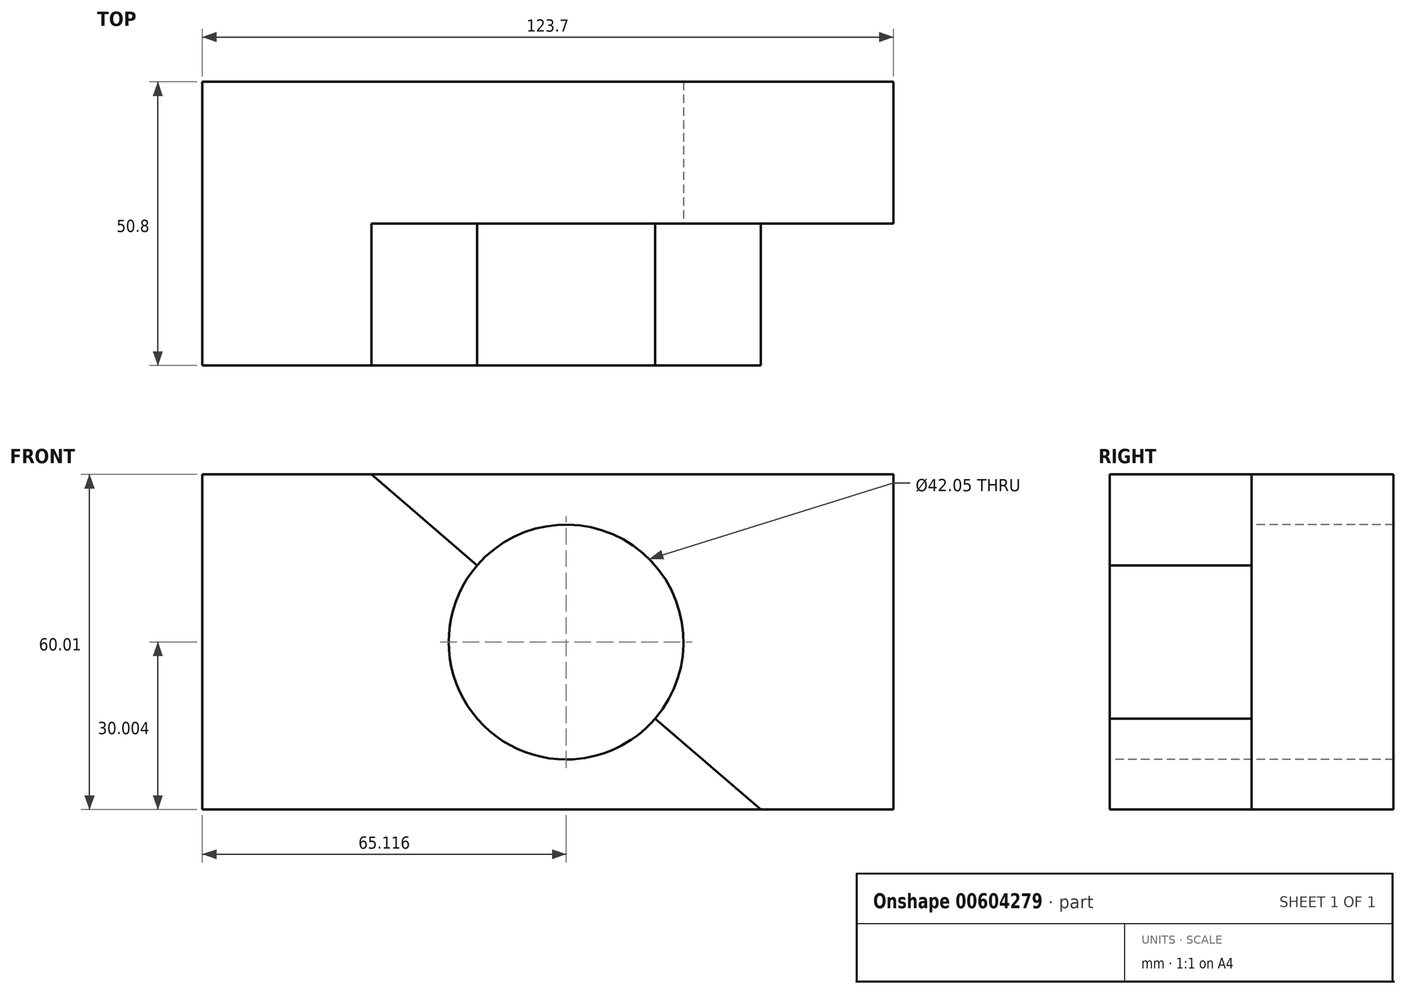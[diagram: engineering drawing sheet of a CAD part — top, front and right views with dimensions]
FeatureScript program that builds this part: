
annotation { "Feature Type Name" : "Feature", "Feature Type Description" : "" }
export const myFeature = defineFeature(function(context is Context, id is Id, definition is map)
    precondition{}
    {
        {
            var Q0;
            Q0=qCreatedBy(makeId("Front.planeOp"),FACE);
            var sketch = newSketch(context, id + "F0", { "sketchPlane" : qUnion([Q0])});
            skLineSegment(sketch, "E0.bottom", {"start": v(-74.58, 0) * mm, "end": v(23.72, 0) * mm});
            skLineSegment(sketch, "E0.top", {"start": v(-74.58, 60) * mm, "end": v(23.72, 60) * mm});
            skLineSegment(sketch, "E0.left", {"start": v(-74.58, 0) * mm, "end": v(-74.58, 60) * mm});
            skLineSegment(sketch, "E0.right", {"start": v(23.72, 0) * mm, "end": v(23.72, 60) * mm});
            skSolve(sketch);
        }
        {
            var Q0;
            Q0=makeQuery(id+"F0.imprint","IMPRINT",FACE,{"disambiguationData":[TD([[makeQuery(id+"F0.imprint","IMPRINT",EDGE,{"derivedFrom":sQuery(id+"F0.wireOp",EDGE,"E0.bottom")}),1.0]])]});
            extrude(context, id + "F1", {"entities" : qUnion([Q0]), "depth" : 25.4 * mm, "offsetDistance" : 25.4 * mm});
        }
        {
            var Q0;
            Q0=makeQuery(id+"F1.opExtrude","CAP_FACE",FACE,{"disambiguationData":[OSD([sQuery(id+"F0.wireOp",EDGE,"E0.bottom"),sQuery(id+"F0.wireOp",EDGE,"E0.top"),sQuery(id+"F0.wireOp",EDGE,"E0.left"),sQuery(id+"F0.wireOp",EDGE,"E0.right")])],"isStart":false});
            extrude(context, id + "F2", {"entities" : qUnion([Q0]), "operationType" : NewBodyOperationType.ADD, "depth" : 25.4 * mm, "offsetDistance" : 25.4 * mm});
        }
        {
            var Q0;
            {var subQ0=sQuery(id+"F0.wireOp",EDGE,"E0.left");Q0=makeQuery(id+"F2.boolean.opBoolean","MERGE",FACE,{"derivedFrom":[makeQuery(id+"F1.opExtrude","SWEPT_FACE",FACE,{"disambiguationData":[OSD([subQ0])]}),makeQuery(id+"F2.opExtrude","SWEPT_FACE",FACE,{"disambiguationData":[OSD([subQ0])]})]});}
            extrude(context, id + "F3", {"entities" : qUnion([Q0]), "operationType" : NewBodyOperationType.ADD, "depth" : 25.4 * mm, "offsetDistance" : 25.4 * mm});
        }
        {
            var Q0;
            {var subQ0=sQuery(id+"F0.wireOp",EDGE,"E0.left");Q0=makeQuery(id+"F3.boolean.opBoolean","MERGE",FACE,{"derivedFrom":[makeQuery(id+"F2.opExtrude","CAP_FACE",FACE,{"disambiguationData":[OSD([sQuery(id+"F0.wireOp",EDGE,"E0.bottom"),sQuery(id+"F0.wireOp",EDGE,"E0.top"),subQ0,sQuery(id+"F0.wireOp",EDGE,"E0.right")])],"isStart":false}),makeQuery(id+"F3.opExtrude","SWEPT_FACE",FACE,{"disambiguationData":[OSD([subQ0]),TDD([makeQuery(id+"F2.opExtrude","CAP_EDGE",EDGE,{"disambiguationData":[OSD([subQ0])],"isStart":false})])]})]});}
            var sketch = newSketch(context, id + "F4", { "sketchPlane" : qUnion([Q0])});
            skLineSegment(sketch, "E1", {"start": v(-69.73, 60) * mm, "end": v(0, 0) * mm});
            skSolve(sketch);
        }
        {
            var Q0;
            {var subQ0=sQuery(id+"F4.wireOp",EDGE,"E1");Q0=makeQuery(id+"F4.imprint","IMPRINT",FACE,{"disambiguationData":[TD([[makeQuery(id+"F4.imprint","IMPRINT",EDGE,{"derivedFrom":subQ0}),1.0]])]});}
            extrude(context, id + "F5", {"entities" : qUnion([Q0]), "operationType" : NewBodyOperationType.REMOVE, "oppositeDirection" : true, "depth" : 25.4 * mm, "offsetDistance" : 25.4 * mm});
        }
        {
            var Q0;
            {var subQ0=sQuery(id+"F0.wireOp",EDGE,"E0.left");Q0=makeQuery(id+"F3.boolean.opBoolean","MERGE",FACE,{"derivedFrom":[makeQuery(id+"F2.opExtrude","CAP_FACE",FACE,{"disambiguationData":[OSD([sQuery(id+"F0.wireOp",EDGE,"E0.bottom"),sQuery(id+"F0.wireOp",EDGE,"E0.top"),subQ0,sQuery(id+"F0.wireOp",EDGE,"E0.right")])],"isStart":false}),makeQuery(id+"F3.opExtrude","SWEPT_FACE",FACE,{"disambiguationData":[OSD([subQ0]),TDD([makeQuery(id+"F2.opExtrude","CAP_EDGE",EDGE,{"disambiguationData":[OSD([subQ0])],"isStart":false})])]})]});}
            var sketch = newSketch(context, id + "F6", { "sketchPlane" : qUnion([Q0])});
            skCircle(sketch, "E2", {"center": v(-34.86, 30) * mm, "radius": 21.03 * mm});
            skSolve(sketch);
        }
        {
            var Q0;
            {var subQ0=sQuery(id+"F6.wireOp",EDGE,"E2");var subQ1=makeQuery(id+"F5.boolean.opBoolean","COPY",EDGE,{"derivedFrom":makeQuery(id+"F5.opExtrude","CAP_EDGE",EDGE,{"disambiguationData":[OSD([sQuery(id+"F4.wireOp",EDGE,"E1")])],"isStart":true})});var subQ2=makeQuery(id+"F6.imprint","INTERSECT",VERTEX,{"disambiguationData":[OD(0.0)],"derivedFrom":[subQ1,subQ0]});Q0=makeQuery(id+"F6.imprint","IMPRINT",FACE,{"disambiguationData":[TD([[makeQuery(id+"F6.imprint","IMPRINT",EDGE,{"disambiguationData":[TD([[subQ2,-1.0]])],"derivedFrom":subQ0}),1.0]])]});}
            var Q1;
            {var subQ0=sQuery(id+"F6.wireOp",EDGE,"E2");var subQ1=makeQuery(id+"F5.boolean.opBoolean","COPY",EDGE,{"derivedFrom":makeQuery(id+"F5.opExtrude","CAP_EDGE",EDGE,{"disambiguationData":[OSD([sQuery(id+"F4.wireOp",EDGE,"E1")])],"isStart":true})});var subQ2=makeQuery(id+"F6.imprint","INTERSECT",VERTEX,{"disambiguationData":[OD(0.0)],"derivedFrom":[subQ1,subQ0]});Q1=makeQuery(id+"F6.imprint","IMPRINT",FACE,{"disambiguationData":[TD([[makeQuery(id+"F6.imprint","IMPRINT",EDGE,{"disambiguationData":[TD([[subQ2,1.0]])],"derivedFrom":subQ0}),1.0]])]});}
            extrude(context, id + "F7", {"entities" : qUnion([Q0, Q1]), "operationType" : NewBodyOperationType.REMOVE, "oppositeDirection" : true, "depth" : 58.17 * mm, "offsetDistance" : 25.4 * mm});
        }
    });
